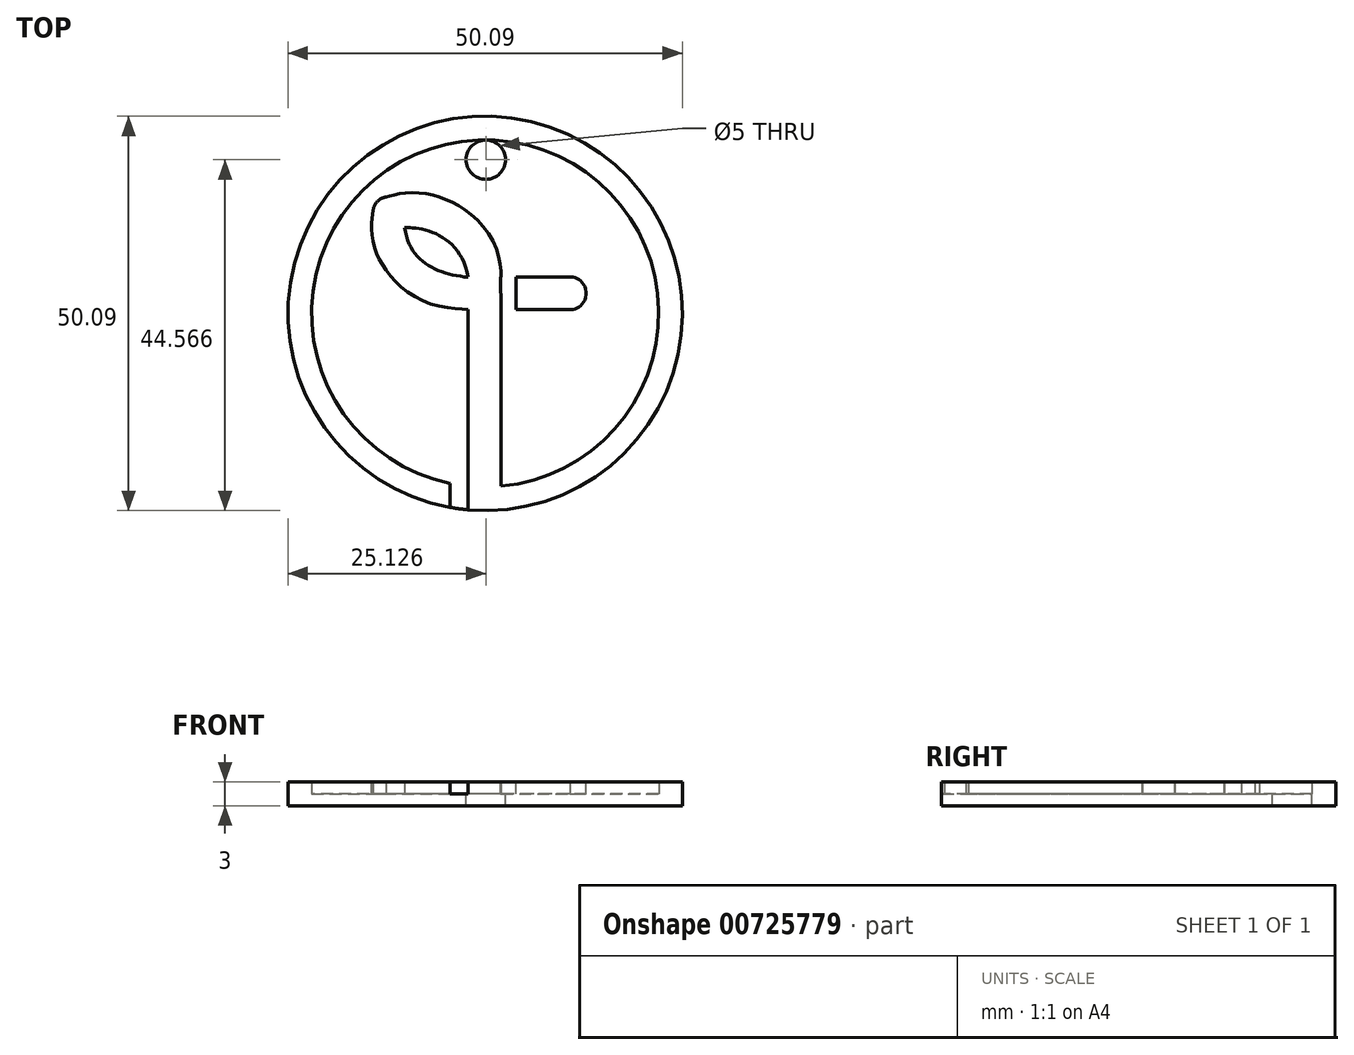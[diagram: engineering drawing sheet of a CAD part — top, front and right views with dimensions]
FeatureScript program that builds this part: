
annotation { "Feature Type Name" : "Feature", "Feature Type Description" : "" }
export const myFeature = defineFeature(function(context is Context, id is Id, definition is map)
    precondition{}
    {
        {
            var Q0;
            Q0=qCreatedBy(makeId("Top.planeOp"),FACE);
            var sketch = newSketch(context, id + "F0", { "sketchPlane" : qUnion([Q0])});
            skCircle(sketch, "E0", {"center": v(1.03, 1.94) * mm, "radius": 25.05 * mm});
            skPoint(sketch, "E0.first.point", {"position": v(-24.01, 1.98) * mm});
            skPoint(sketch, "E0.second.point", {"position": v(20.87, 17.23) * mm});
            skPoint(sketch, "E0.third.point", {"position": v(1.08, -23.1) * mm});
            skCircle(sketch, "E1.0", {"center": v(1.03, 1.94) * mm, "radius": 22.05 * mm});
            skLineSegment(sketch, "E2", {"start": v(11.81, 3.42) * mm, "end": v(2.06, 3.42) * mm, "construction": true});
            skLineSegment(sketch, "E3", {"start": v(2.06, 3.42) * mm, "end": v(2.06, -20.76) * mm, "construction": true});
            skLineSegment(sketch, "E4", {"start": v(2.06, -20.76) * mm, "end": v(-0.13, -20.76) * mm, "construction": true});
            skLineSegment(sketch, "E5", {"start": v(-0.13, -20.76) * mm, "end": v(-0.13, 3.42) * mm, "construction": true});
            skLineSegment(sketch, "E6", {"start": v(11.81, 5.56) * mm, "end": v(2.06, 5.56) * mm, "construction": true});
            skFitSpline(sketch, "E7", {"points": [v(2.06, 5.56) * mm, v(-11.33, 15.76) * mm], "startDerivative": vector(-0.3, 18.87) * mm, "endDerivative": vector(-23.3, -6.12) * mm, "construction": true});
            skFitSpline(sketch, "E8", {"points": [v(-0.13, 3.42) * mm, v(-12.22, 14.82) * mm], "startDerivative": vector(-24.73, 0.93) * mm, "endDerivative": vector(2.98, 18.55) * mm, "construction": true});
            skFitSpline(sketch, "E9", {"points": [v(11.81, 5.56) * mm, v(11.81, 3.42) * mm], "startDerivative": vector(3.97, 0) * mm, "endDerivative": vector(-3.97, 0) * mm, "construction": true});
            skFitSpline(sketch, "E10", {"points": [v(-12.22, 14.82) * mm, v(-11.33, 15.76) * mm], "startDerivative": vector(0.28, 1.73) * mm, "endDerivative": vector(1.34, 0.35) * mm, "construction": true});
            skFitSpline(sketch, "E11", {"points": [v(-1.13, 6.53) * mm, v(-9.2, 12.84) * mm], "startDerivative": vector(-2.6, 16) * mm, "endDerivative": vector(-7.16, -0.33) * mm});
            skFitSpline(sketch, "E12", {"points": [v(-9.2, 12.84) * mm, v(-1.13, 6.53) * mm], "startDerivative": vector(1.8, -13.32) * mm, "endDerivative": vector(11.4, -1.13) * mm});
            skLineSegment(sketch, "E13.0", {"start": v(11.81, 2.42) * mm, "end": v(3.06, 2.42) * mm});
            skFitSpline(sketch, "E13.1", {"points": [v(11.81, 6.56) * mm, v(11.96, 6.56) * mm, v(12.26, 6.53) * mm, v(12.68, 6.39) * mm, v(13.05, 6.16) * mm, v(13.44, 5.77) * mm, v(13.73, 5.2) * mm, v(13.84, 4.5) * mm, v(13.73, 3.78) * mm, v(13.44, 3.21) * mm, v(13.05, 2.82) * mm, v(12.68, 2.6) * mm, v(12.26, 2.45) * mm, v(11.96, 2.42) * mm, v(11.81, 2.42) * mm]});
            skLineSegment(sketch, "E13.2", {"start": v(3.06, 2.42) * mm, "end": v(3.06, -21.76) * mm});
            skLineSegment(sketch, "E13.3", {"start": v(11.81, 6.56) * mm, "end": v(3, 6.56) * mm});
            skFitSpline(sketch, "E13.4", {"points": [v(3.06, 5.58) * mm, v(3.04, 7.3) * mm, v(2.24, 10.66) * mm, v(-0.33, 14.13) * mm, v(-3.2, 16.06) * mm, v(-5.7, 16.99) * mm, v(-8.52, 17.28) * mm, v(-10.55, 17) * mm, v(-11.59, 16.72) * mm]});
            skLineSegment(sketch, "E13.5", {"start": v(3.06, -21.76) * mm, "end": v(-1.13, -21.76) * mm});
            skLineSegment(sketch, "E13.6", {"start": v(-1.13, -21.76) * mm, "end": v(-1.13, 2.48) * mm});
            skFitSpline(sketch, "E13.7", {"points": [v(-0.17, 2.42) * mm, v(-2.33, 2.5) * mm, v(-6.23, 3.27) * mm, v(-9.9, 5.53) * mm, v(-11.93, 8) * mm, v(-12.95, 10.12) * mm, v(-13.42, 12.47) * mm, v(-13.34, 14.13) * mm, v(-13.2, 14.98) * mm]});
            skFitSpline(sketch, "E13.8", {"points": [v(-13.2, 14.98) * mm, v(-13.17, 15.2) * mm, v(-13.04, 15.66) * mm, v(-12.62, 16.22) * mm, v(-12.1, 16.57) * mm, v(-11.75, 16.68) * mm, v(-11.59, 16.72) * mm]});
            skFitSpline(sketch, "E14.0", {"points": [v(-9.28, 13.7) * mm, v(-9.25, 13.02) * mm, v(-9.07, 11.78) * mm, v(-8.46, 10.29) * mm, v(-7.57, 9.1) * mm, v(-6.42, 8.15) * mm, v(-5.04, 7.42) * mm, v(-2.97, 6.73) * mm, v(-1.24, 6.5) * mm, v(-0.1, 6.46) * mm], "construction": true});
            skFitSpline(sketch, "E14.1", {"points": [v(-1.03, 5.52) * mm, v(-1.07, 6.26) * mm, v(-1.3, 7.61) * mm, v(-1.98, 9.24) * mm, v(-2.96, 10.53) * mm, v(-4.58, 11.85) * mm, v(-7.06, 12.8) * mm, v(-9.14, 12.89) * mm, v(-10.08, 12.78) * mm], "construction": true});
            skSolve(sketch);
        }
        {
            var Q0;
            Q0=makeQuery(id+"F0.imprint","IMPRINT",FACE,{"disambiguationData":[TD([[makeQuery(id+"F0.imprint","IMPRINT",EDGE,{"derivedFrom":sQuery(id+"F0.wireOp",EDGE,"E0")}),1.0]])]});
            var Q1;
            Q1=makeQuery(id+"F0.imprint","IMPRINT",FACE,{"disambiguationData":[TD([[makeQuery(id+"F0.imprint","IMPRINT",EDGE,{"derivedFrom":sQuery(id+"F0.wireOp",EDGE,"E11")}),-1.0]])]});
            var Q2;
            {var subQ5=sQuery(id+"F0.wireOp",EDGE,"E13.5");Q2=makeQuery(id+"F0.imprint","IMPRINT",FACE,{"disambiguationData":[TD([[makeQuery(id+"F0.imprint","IMPRINT",EDGE,{"derivedFrom":subQ5}),-1.0]])]});}
            extrude(context, id + "F1", {"entities" : qUnion([Q0, Q1, Q2]), "depth" : 3 * mm, "offsetDistance" : 25 * mm});
        }
        {
            var Q0;
            {var subQ0=sQuery(id+"F0.wireOp",EDGE,"E13.0");Q0=makeQuery(id+"F0.imprint","IMPRINT",FACE,{"disambiguationData":[TD([[makeQuery(id+"F0.imprint","IMPRINT",EDGE,{"derivedFrom":subQ0}),1.0]])]});}
            var Q1;
            Q1=makeQuery(id+"F0.imprint","IMPRINT",FACE,{"disambiguationData":[TD([[makeQuery(id+"F0.imprint","IMPRINT",EDGE,{"derivedFrom":sQuery(id+"F0.wireOp",EDGE,"E11")}),1.0]])]});
            extrude(context, id + "F2", {"entities" : qUnion([Q0, Q1]), "operationType" : NewBodyOperationType.ADD, "depth" : 1.5 * mm, "offsetDistance" : 25 * mm});
        }
        {
            var Q0;
            Q0=makeQuery(id+"F1.opExtrude","CAP_FACE",FACE,{"disambiguationData":[OSD([sQuery(id+"F0.wireOp",EDGE,"E0"),sQuery(id+"F0.wireOp",EDGE,"E1.0"),sQuery(id+"F0.wireOp",EDGE,"E11"),sQuery(id+"F0.wireOp",EDGE,"E12"),sQuery(id+"F0.wireOp",EDGE,"E13.0"),sQuery(id+"F0.wireOp",EDGE,"E13.1"),sQuery(id+"F0.wireOp",EDGE,"E13.2"),sQuery(id+"F0.wireOp",EDGE,"E13.3"),sQuery(id+"F0.wireOp",EDGE,"E13.4"),sQuery(id+"F0.wireOp",EDGE,"E13.6"),sQuery(id+"F0.wireOp",EDGE,"E13.7"),sQuery(id+"F0.wireOp",EDGE,"E13.8")])],"isStart":false});
            var sketch = newSketch(context, id + "F3", { "sketchPlane" : qUnion([Q0])});
            skLineSegment(sketch, "E15.bottom", {"start": v(3, 6.56) * mm, "end": v(4.95, 6.56) * mm});
            skLineSegment(sketch, "E15.top", {"start": v(3.06, 2.42) * mm, "end": v(4.95, 2.42) * mm});
            skLineSegment(sketch, "E15.left", {"start": v(3, 6.56) * mm, "end": v(3.06, 2.42) * mm});
            skLineSegment(sketch, "E15.right", {"start": v(4.95, 6.56) * mm, "end": v(4.95, 2.42) * mm});
            skLineSegment(sketch, "E16.bottom", {"start": v(-1.13, -18.66) * mm, "end": v(-3.45, -18.66) * mm});
            skLineSegment(sketch, "E16.top", {"start": v(-1.13, -24.39) * mm, "end": v(-3.45, -24.39) * mm});
            skLineSegment(sketch, "E16.left", {"start": v(-1.13, -18.66) * mm, "end": v(-1.13, -24.39) * mm});
            skLineSegment(sketch, "E16.right", {"start": v(-3.45, -18.66) * mm, "end": v(-3.45, -24.39) * mm});
            skSolve(sketch);
        }
        {
            var Q0;
            Q0 = qSketchRegion(id + "F3", true);
            extrude(context, id + "F4", {"entities" : qUnion([Q0]), "operationType" : NewBodyOperationType.REMOVE, "oppositeDirection" : true, "depth" : 1.5 * mm, "offsetDistance" : 25 * mm});
        }
        {
            var Q0;
            Q0=makeQuery(id+"F4.boolean.opBoolean","MERGE",FACE,{"derivedFrom":[makeQuery(id+"F2.opExtrude","CAP_FACE",FACE,{"disambiguationData":[OSD([sQuery(id+"F0.wireOp",EDGE,"E1.0"),sQuery(id+"F0.wireOp",EDGE,"E13.0"),sQuery(id+"F0.wireOp",EDGE,"E13.1"),sQuery(id+"F0.wireOp",EDGE,"E13.2"),sQuery(id+"F0.wireOp",EDGE,"E13.3"),sQuery(id+"F0.wireOp",EDGE,"E13.4"),sQuery(id+"F0.wireOp",EDGE,"E13.6"),sQuery(id+"F0.wireOp",EDGE,"E13.7"),sQuery(id+"F0.wireOp",EDGE,"E13.8")])],"isStart":false}),makeQuery(id+"F4.opExtrude","CAP_FACE",FACE,{"disambiguationData":[OSD([sQuery(id+"F3.wireOp",EDGE,"E15.bottom"),sQuery(id+"F3.wireOp",EDGE,"E15.top"),sQuery(id+"F3.wireOp",EDGE,"E15.left"),sQuery(id+"F3.wireOp",EDGE,"E15.right")])],"isStart":false}),makeQuery(id+"F4.opExtrude","CAP_FACE",FACE,{"disambiguationData":[OSD([sQuery(id+"F3.wireOp",EDGE,"E16.bottom"),sQuery(id+"F3.wireOp",EDGE,"E16.top"),sQuery(id+"F3.wireOp",EDGE,"E16.left"),sQuery(id+"F3.wireOp",EDGE,"E16.right")])],"isStart":false})]});
            var sketch = newSketch(context, id + "F5", { "sketchPlane" : qUnion([Q0])});
            skCircle(sketch, "E17", {"center": v(1.12, 21.47) * mm, "radius": 2.5 * mm});
            skSolve(sketch);
        }
        {
            var Q0;
            Q0 = qSketchRegion(id + "F5", true);
            extrude(context, id + "F6", {"entities" : qUnion([Q0]), "operationType" : NewBodyOperationType.REMOVE, "endBound" : BoundingType.THROUGH_ALL, "oppositeDirection" : true, "depth" : 25 * mm, "offsetDistance" : 25 * mm});
        }
    });
